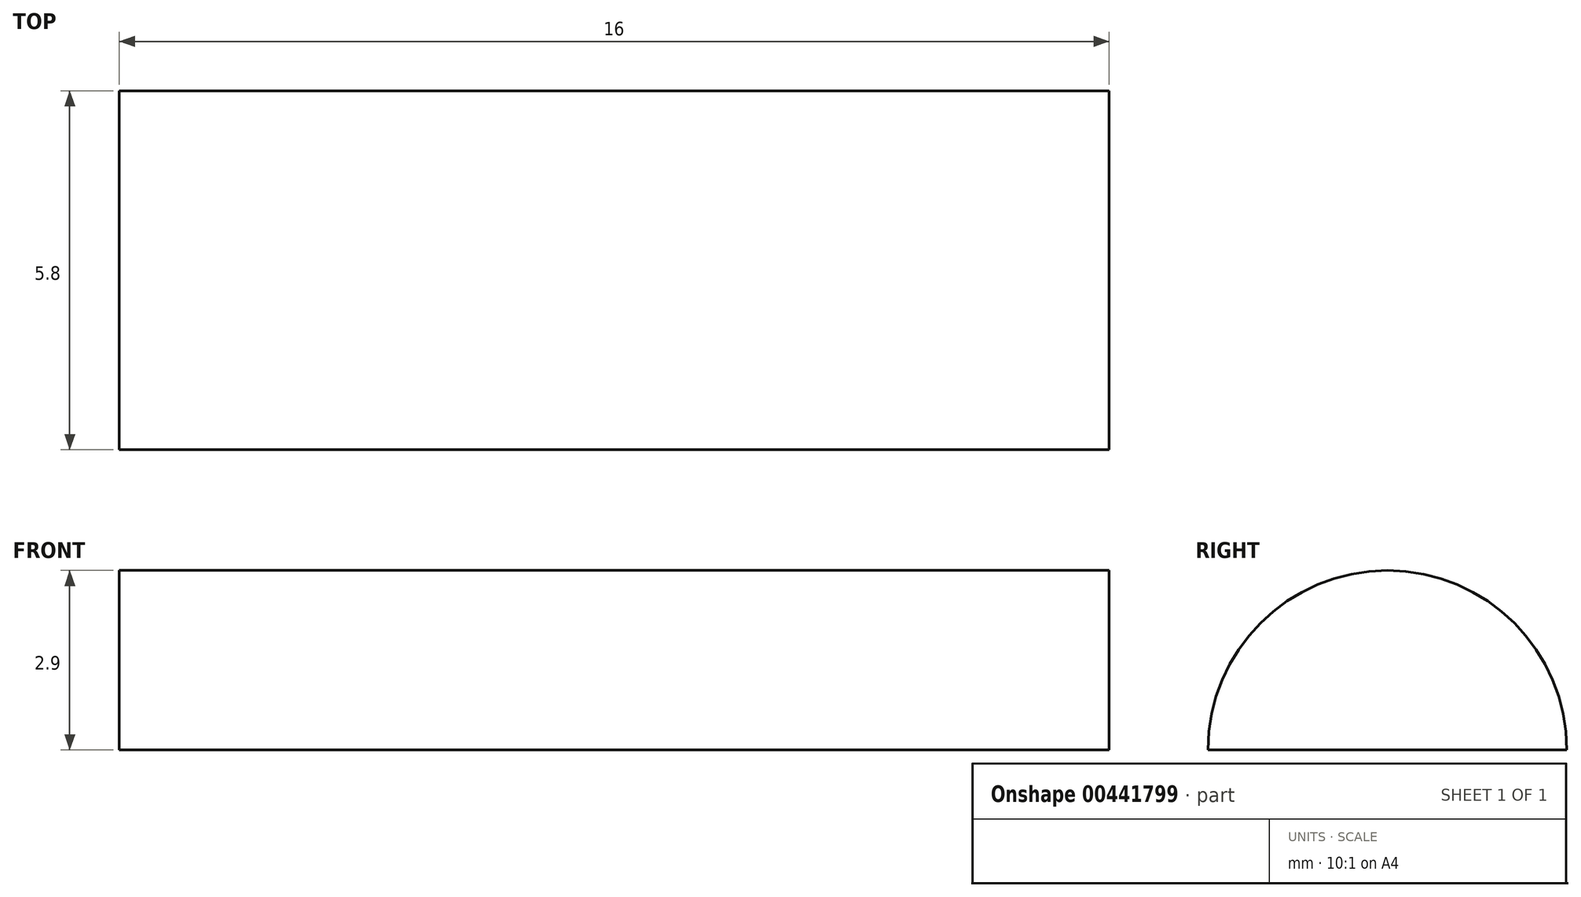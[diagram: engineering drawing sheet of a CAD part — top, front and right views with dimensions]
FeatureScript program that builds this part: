
annotation { "Feature Type Name" : "Feature", "Feature Type Description" : "" }
export const myFeature = defineFeature(function(context is Context, id is Id, definition is map)
    precondition{}
    {
        {
            var Q0;
            Q0=qCreatedBy(makeId("Right.planeOp"),FACE);
            var sketch = newSketch(context, id + "F0", { "sketchPlane" : qUnion([Q0])});
            skArc(sketch, "E0", {"start": v(2.9, 0) * mm, "mid": v(0, 2.9) * mm, "end": v(-2.9, 0) * mm});
            skLineSegment(sketch, "E1", {"start": v(-2.9, 0) * mm, "end": v(2.9, 0) * mm});
            skSolve(sketch);
        }
        {
            var Q0;
            Q0=makeQuery(id+"F0.imprint","IMPRINT",FACE,{"disambiguationData":[TD([[makeQuery(id+"F0.imprint","IMPRINT",EDGE,{"derivedFrom":sQuery(id+"F0.wireOp",EDGE,"E0")}),1.0]])]});
            extrude(context, id + "F1", {"entities" : qUnion([Q0]), "depth" : 16 * mm});
        }
    });
